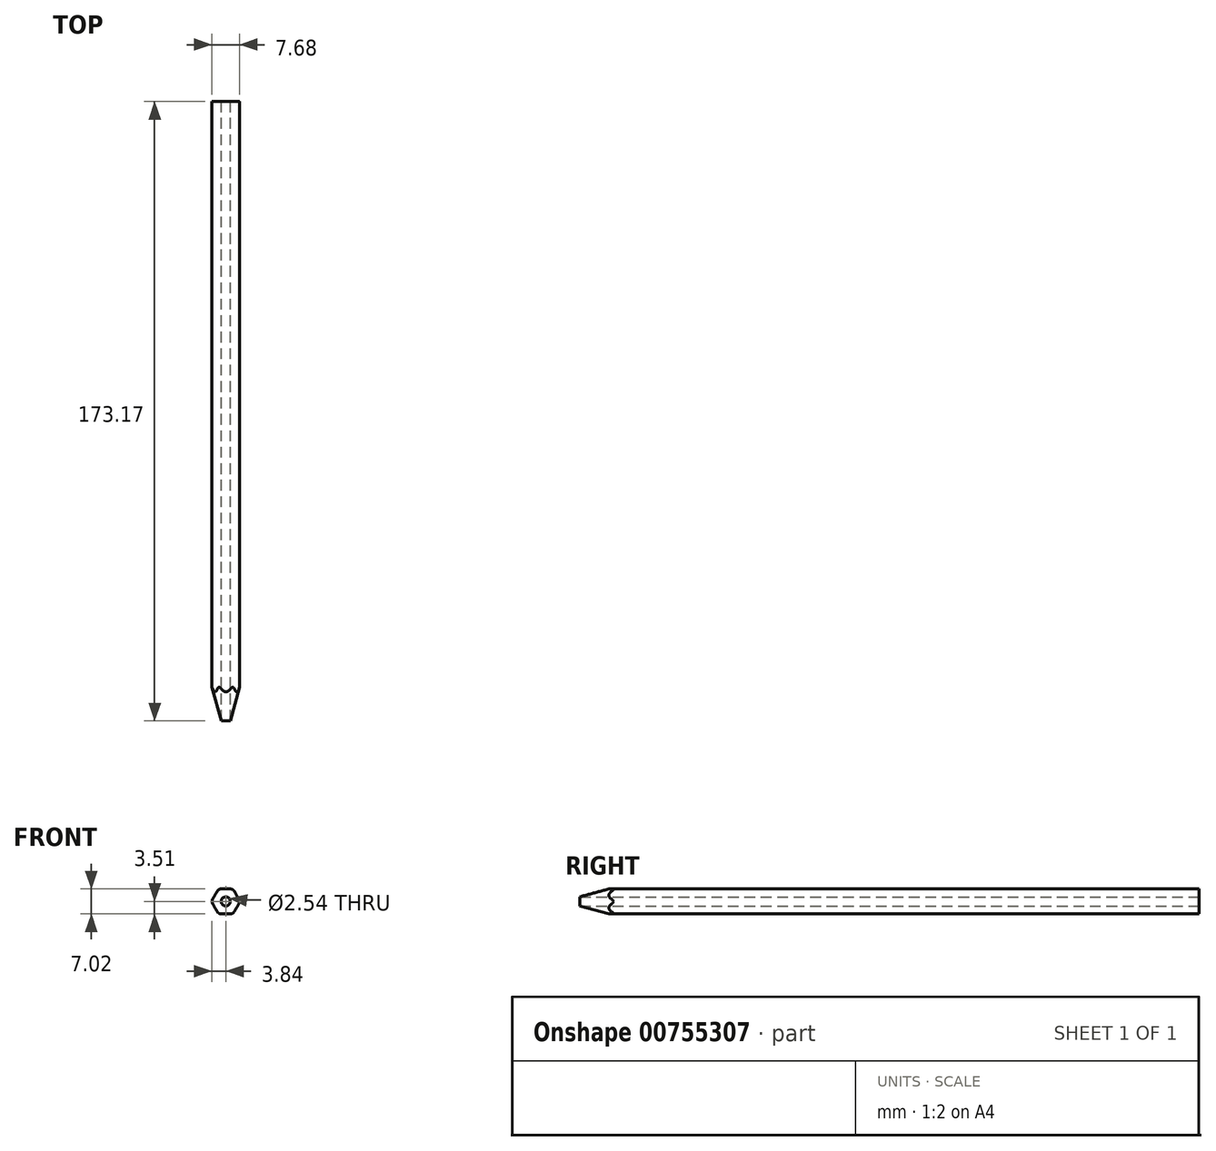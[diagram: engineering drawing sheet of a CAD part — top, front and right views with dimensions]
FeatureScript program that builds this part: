
annotation { "Feature Type Name" : "Feature", "Feature Type Description" : "" }
export const myFeature = defineFeature(function(context is Context, id is Id, definition is map)
    precondition{}
    {
        {
            var Q0;
            Q0=qCreatedBy(makeId("Front.planeOp"),FACE);
            var sketch = newSketch(context, id + "F0", { "sketchPlane" : qUnion([Q0])});
            skCircle(sketch, "E0.cCircle", {"center": v(0, 0) * mm, "radius": 3.5 * mm, "construction": true});
            skLineSegment(sketch, "E0.0", {"start": v(2.06, 3.47) * mm, "end": v(4.03, -0.05) * mm});
            skLineSegment(sketch, "E0.1", {"start": v(4.03, -0.05) * mm, "end": v(1.97, -3.52) * mm});
            skLineSegment(sketch, "E0.2", {"start": v(1.97, -3.52) * mm, "end": v(-2.06, -3.47) * mm});
            skLineSegment(sketch, "E0.3", {"start": v(-2.06, -3.47) * mm, "end": v(-4.03, 0.05) * mm});
            skLineSegment(sketch, "E0.4", {"start": v(-4.03, 0.05) * mm, "end": v(-1.97, 3.52) * mm});
            skLineSegment(sketch, "E0.5", {"start": v(-1.97, 3.52) * mm, "end": v(2.06, 3.47) * mm});
            skPoint(sketch, "E0.0.midPoint", {"position": v(3.05, 1.7) * mm});
            skCircle(sketch, "E1", {"center": v(0, 0) * mm, "radius": 1.27 * mm});
            skSolve(sketch);
        }
        {
            var Q0;
            Q0=makeQuery(id+"F0.imprint","IMPRINT",FACE,{"disambiguationData":[TD([[makeQuery(id+"F0.imprint","IMPRINT",EDGE,{"derivedFrom":sQuery(id+"F0.wireOp",EDGE,"E0.0")}),-1.0]])]});
            extrude(context, id + "F1", {"entities" : qUnion([Q0]), "depth" : 177.8 * mm, "offsetDistance" : 25.4 * mm, "symmetric" : true});
        }
        {
            var Q0;
            Q0=qCreatedBy(makeId("Top.planeOp"),FACE);
            var sketch = newSketch(context, id + "F2", { "sketchPlane" : qUnion([Q0])});
            skLineSegment(sketch, "E2", {"start": v(0, -88.9) * mm, "end": v(-4.03, -74.2) * mm});
            skLineSegment(sketch, "E3", {"start": v(-7.65, -88.9) * mm, "end": v(27.36, -88.9) * mm, "construction": true});
            skLineSegment(sketch, "E4", {"start": v(0, -88.9) * mm, "end": v(0, -70.87) * mm, "construction": true});
            skLineSegment(sketch, "E5", {"start": v(-4.03, -74.2) * mm, "end": v(-4.03, -99.68) * mm});
            skLineSegment(sketch, "E6", {"start": v(0, -88.9) * mm, "end": v(0, -99.68) * mm});
            skLineSegment(sketch, "E7", {"start": v(0, -99.68) * mm, "end": v(-4.03, -99.68) * mm});
            skSolve(sketch);
        }
        {
            var Q0;
            Q0=makeQuery(id+"F2.imprint","IMPRINT",FACE,{"disambiguationData":[TD([[makeQuery(id+"F2.imprint","IMPRINT",EDGE,{"derivedFrom":sQuery(id+"F2.wireOp",EDGE,"E2")}),1.0]])]});
            var sketch = newSketch(context, id + "F3", { "sketchPlane" : qUnion([Q0])});
            skLineSegment(sketch, "E8", {"start": v(0, -50.25) * mm, "end": v(0, -101.84) * mm, "construction": true});
            skSolve(sketch);
        }
        {
            var Q0;
            Q0=makeQuery(id+"F2.imprint","IMPRINT",FACE,{"disambiguationData":[TD([[makeQuery(id+"F2.imprint","IMPRINT",EDGE,{"derivedFrom":sQuery(id+"F2.wireOp",EDGE,"E2")}),1.0]])]});
            var Q1;
            Q1=sQuery(id+"F3.wireOp",EDGE,"E8");
            revolve(context, id + "F4", {"operationType" : NewBodyOperationType.REMOVE, "surfaceOperationType" : NewSurfaceOperationType.NEW, "entities" : qUnion([Q0]), "axis" : qUnion([Q1]), "revolveType" : RevolveType.FULL, "oppositeDirection" : true});
        }
        {
            var Q0;
            Q0=makeQuery(id+"F1.opExtrude","SWEPT_EDGE",EDGE,{"disambiguationData":[OSD([sQuery(id+"F0.wireOp",EDGE,"E0.0"),sQuery(id+"F0.wireOp",EDGE,"E0.5")])]});
            var Q1;
            Q1=makeQuery(id+"F1.opExtrude","SWEPT_EDGE",EDGE,{"disambiguationData":[OSD([sQuery(id+"F0.wireOp",EDGE,"E0.4"),sQuery(id+"F0.wireOp",EDGE,"E0.5")])]});
            var Q2;
            Q2=makeQuery(id+"F1.opExtrude","SWEPT_EDGE",EDGE,{"disambiguationData":[OSD([sQuery(id+"F0.wireOp",EDGE,"E0.3"),sQuery(id+"F0.wireOp",EDGE,"E0.4")])]});
            var Q3;
            Q3=makeQuery(id+"F1.opExtrude","SWEPT_EDGE",EDGE,{"disambiguationData":[OSD([sQuery(id+"F0.wireOp",EDGE,"E0.2"),sQuery(id+"F0.wireOp",EDGE,"E0.3")])]});
            var Q4;
            Q4=makeQuery(id+"F1.opExtrude","SWEPT_EDGE",EDGE,{"disambiguationData":[OSD([sQuery(id+"F0.wireOp",EDGE,"E0.1"),sQuery(id+"F0.wireOp",EDGE,"E0.2")])]});
            var Q5;
            Q5=makeQuery(id+"F1.opExtrude","SWEPT_EDGE",EDGE,{"disambiguationData":[OSD([sQuery(id+"F0.wireOp",EDGE,"E0.0"),sQuery(id+"F0.wireOp",EDGE,"E0.1")])]});
            fillet(context, id + "F5", {"entities" : qUnion([Q0, Q1, Q2, Q3, Q4, Q5]), "radius" : 1.27 * mm, "tangentPropagation" : true, "allowEdgeOverflow" : false});
        }
    });
